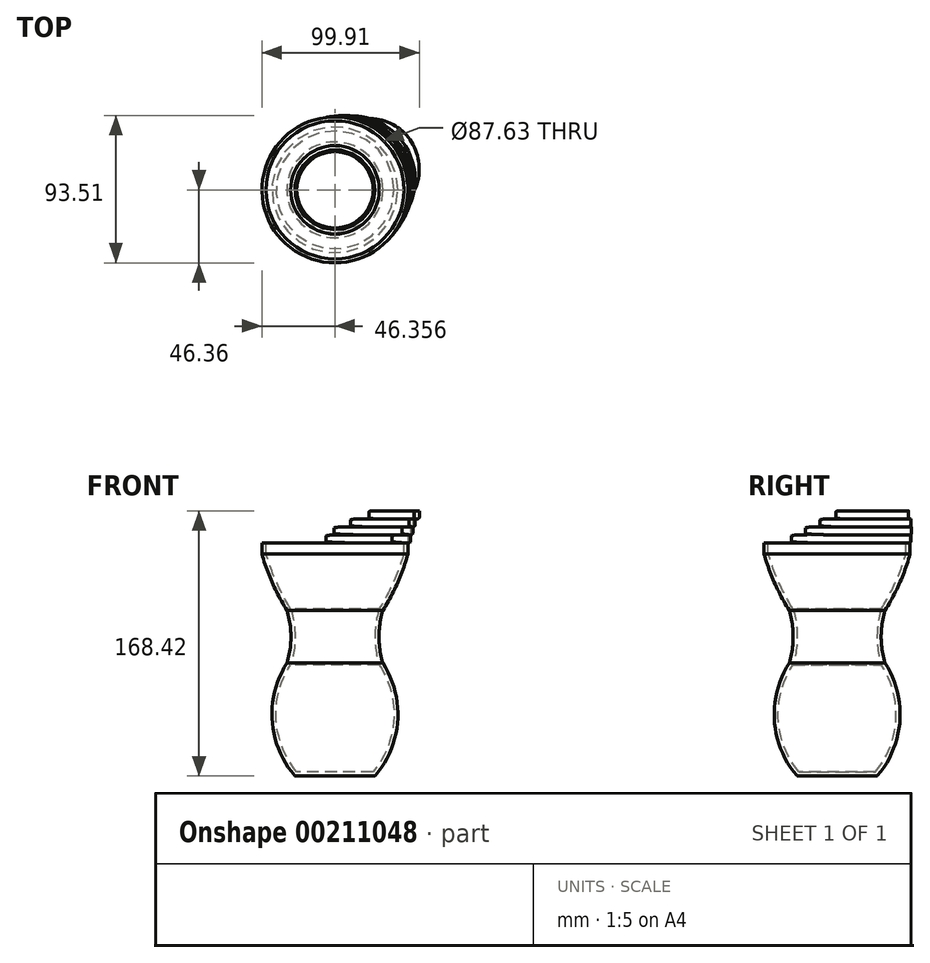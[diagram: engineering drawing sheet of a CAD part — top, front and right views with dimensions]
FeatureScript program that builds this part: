
annotation { "Feature Type Name" : "Feature", "Feature Type Description" : "" }
export const myFeature = defineFeature(function(context is Context, id is Id, definition is map)
    precondition{}
    {
        {
            var Q0;
            Q0=qCreatedBy(makeId("Front.planeOp"),FACE);
            var sketch = newSketch(context, id + "F0", { "sketchPlane" : qUnion([Q0])});
            skLineSegment(sketch, "E0", {"start": v(-425.9, -19.23) * mm, "end": v(-425.9, -160.2) * mm});
            skLineSegment(sketch, "E1", {"start": v(-425.9, -160.2) * mm, "end": v(-451.3, -160.2) * mm});
            skLineSegment(sketch, "E2", {"start": v(-472.26, -19.23) * mm, "end": v(-425.9, -19.23) * mm});
            skArc(sketch, "E3", {"start": v(-456.34, -88.54) * mm, "mid": v(-453.84, -71.81) * mm, "end": v(-456.34, -55.09) * mm});
            skArc(sketch, "E4", {"start": v(-456.34, -88.54) * mm, "mid": v(-465.76, -125.2) * mm, "end": v(-451.3, -160.2) * mm});
            skArc(sketch, "E5", {"start": v(-472.26, -19.23) * mm, "mid": v(-465.56, -37.72) * mm, "end": v(-456.34, -55.09) * mm});
            skLineSegment(sketch, "E6", {"start": v(-425.9, -19.23) * mm, "end": v(-425.9, -12.1) * mm});
            skLineSegment(sketch, "E7", {"start": v(-472.26, -19.23) * mm, "end": v(-472.26, -12.1) * mm});
            skLineSegment(sketch, "E8", {"start": v(-472.26, -12.1) * mm, "end": v(-425.9, -12.1) * mm});
            skSolve(sketch);
        }
        {
            var Q0;
            Q0=makeQuery(id+"F0.imprint","IMPRINT",FACE,{"disambiguationData":[TD([[makeQuery(id+"F0.imprint","IMPRINT",EDGE,{"derivedFrom":sQuery(id+"F0.wireOp",EDGE,"E0")}),-1.0]])]});
            var Q1;
            Q1=makeQuery(id+"F0.imprint","IMPRINT",FACE,{"disambiguationData":[TD([[makeQuery(id+"F0.imprint","IMPRINT",EDGE,{"derivedFrom":sQuery(id+"F0.wireOp",EDGE,"E2")}),1.0]])]});
            var Q2;
            Q2=sQuery(id+"F0.wireOp",EDGE,"E0");
            revolve(context, id + "F1", {"entities" : qUnion([Q0, Q1]), "axis" : qUnion([Q2]), "revolveType" : RevolveType.FULL});
        }
        {
            var Q0;
            Q0=makeQuery(id+"F1.opRevolve","SWEPT_FACE",FACE,{"disambiguationData":[OSD([sQuery(id+"F0.wireOp",EDGE,"E8")])]});
            shell(context, id + "F2", {"entities" : qUnion([Q0]), "thickness" : 2.54 * mm});
        }
        {
            var Q0;
            Q0=makeQuery(id+"F1.opRevolve","SWEPT_FACE",FACE,{"disambiguationData":[OSD([sQuery(id+"F0.wireOp",EDGE,"E8")])]});
            var sketch = newSketch(context, id + "F3", { "sketchPlane" : qUnion([Q0])});
            skArc(sketch, "E9", {"start": v(-389.73, -29) * mm, "mid": v(-383.55, 23.65) * mm, "end": v(-431.6, 46) * mm});
            skSolve(sketch);
        }
        {
            var Q0;
            {var subQ0=sQuery(id+"F3.wireOp",EDGE,"E9");Q0=makeQuery(id+"F3.imprint","IMPRINT",FACE,{"disambiguationData":[TD([[makeQuery(id+"F3.imprint","IMPRINT",EDGE,{"derivedFrom":subQ0}),1.0]])]});}
            extrude(context, id + "F4", {"entities" : qUnion([Q0]), "depth" : 5.08 * mm});
        }
        {
            var Q0;
            Q0=makeQuery(id+"F4.opExtrude","CAP_FACE",FACE,{"disambiguationData":[OSD([sQuery(id+"F0.wireOp",EDGE,"E7"),sQuery(id+"F0.wireOp",EDGE,"E8"),sQuery(id+"F3.wireOp",EDGE,"E9")])],"isStart":false});
            var sketch = newSketch(context, id + "F5", { "sketchPlane" : qUnion([Q0])});
            skArc(sketch, "E10", {"start": v(-383.3, -20) * mm, "mid": v(-383.5, 27.19) * mm, "end": v(-426.47, 46.7) * mm});
            skSolve(sketch);
        }
        {
            var Q0;
            {var subQ0=sQuery(id+"F5.wireOp",EDGE,"E10");Q0=makeQuery(id+"F5.imprint","IMPRINT",FACE,{"disambiguationData":[TD([[makeQuery(id+"F5.imprint","IMPRINT",EDGE,{"derivedFrom":subQ0}),1.0]])]});}
            extrude(context, id + "F6", {"entities" : qUnion([Q0]), "depth" : 5.08 * mm});
        }
        {
            var Q0;
            Q0=makeQuery(id+"F6.opExtrude","CAP_FACE",FACE,{"disambiguationData":[OSD([sQuery(id+"F3.wireOp",EDGE,"E9"),sQuery(id+"F5.wireOp",EDGE,"E10")])],"isStart":false});
            var sketch = newSketch(context, id + "F7", { "sketchPlane" : qUnion([Q0])});
            skArc(sketch, "E11", {"start": v(-378.91, -10.92) * mm, "mid": v(-381.4, 28.3) * mm, "end": v(-415.99, 46.95) * mm});
            skSolve(sketch);
        }
        {
            var Q0;
            {var subQ0=sQuery(id+"F7.wireOp",EDGE,"E11");Q0=makeQuery(id+"F7.imprint","IMPRINT",FACE,{"disambiguationData":[TD([[makeQuery(id+"F7.imprint","IMPRINT",EDGE,{"derivedFrom":subQ0}),1.0]])]});}
            extrude(context, id + "F8", {"entities" : qUnion([Q0]), "depth" : 5.08 * mm});
        }
        {
            var Q0;
            Q0=makeQuery(id+"F8.opExtrude","CAP_FACE",FACE,{"disambiguationData":[OSD([sQuery(id+"F5.wireOp",EDGE,"E10"),sQuery(id+"F7.wireOp",EDGE,"E11")])],"isStart":false});
            var sketch = newSketch(context, id + "F9", { "sketchPlane" : qUnion([Q0])});
            skArc(sketch, "E12", {"start": v(-375.67, -0.9) * mm, "mid": v(-377.16, 30.22) * mm, "end": v(-404.39, 45.4) * mm});
            skSolve(sketch);
        }
        {
            var Q0;
            {var subQ0=sQuery(id+"F9.wireOp",EDGE,"E12");Q0=makeQuery(id+"F9.imprint","IMPRINT",FACE,{"disambiguationData":[TD([[makeQuery(id+"F9.imprint","IMPRINT",EDGE,{"derivedFrom":subQ0}),1.0]])]});}
            extrude(context, id + "F10", {"entities" : qUnion([Q0]), "depth" : 5.08 * mm});
        }
        {
            var Q0;
            Q0=makeQuery(id+"F6.opExtrude","CAP_EDGE",EDGE,{"disambiguationData":[OSD([sQuery(id+"F3.wireOp",EDGE,"E9")])],"isStart":false});
            var Q1;
            Q1=makeQuery(id+"F4.opExtrude","CAP_EDGE",EDGE,{"disambiguationData":[OSD([sQuery(id+"F0.wireOp",EDGE,"E7"),sQuery(id+"F0.wireOp",EDGE,"E8")])],"isStart":false});
            var Q2;
            Q2=makeQuery(id+"F2.opShell","OFFSET_EDGE",EDGE,{"disambiguationData":[OSD([sQuery(id+"F0.wireOp",EDGE,"E7"),sQuery(id+"F0.wireOp",EDGE,"E8")])]});
            var Q3;
            Q3=makeQuery(id+"F8.opExtrude","CAP_EDGE",EDGE,{"disambiguationData":[OSD([sQuery(id+"F5.wireOp",EDGE,"E10")])],"isStart":false});
            var Q4;
            Q4=makeQuery(id+"F10.opExtrude","CAP_EDGE",EDGE,{"disambiguationData":[OSD([sQuery(id+"F7.wireOp",EDGE,"E11")])],"isStart":false});
            fillet(context, id + "F11", {"entities" : qUnion([Q0, Q1, Q2, Q3, Q4]), "radius" : 0.76 * mm, "tangentPropagation" : true, "allowEdgeOverflow" : false});
        }
        {
            var Q0;
            Q0=makeQuery(id+"F10.opExtrude","CAP_EDGE",EDGE,{"disambiguationData":[OSD([sQuery(id+"F9.wireOp",EDGE,"E12")])],"isStart":true});
            var Q1;
            Q1=makeQuery(id+"F8.opExtrude","CAP_EDGE",EDGE,{"disambiguationData":[OSD([sQuery(id+"F7.wireOp",EDGE,"E11")])],"isStart":true});
            var Q2;
            Q2=makeQuery(id+"F6.opExtrude","CAP_EDGE",EDGE,{"disambiguationData":[OSD([sQuery(id+"F5.wireOp",EDGE,"E10")])],"isStart":true});
            var Q3;
            Q3=makeQuery(id+"F4.opExtrude","CAP_EDGE",EDGE,{"disambiguationData":[OSD([sQuery(id+"F3.wireOp",EDGE,"E9")])],"isStart":true});
            fillet(context, id + "F12", {"entities" : qUnion([Q0, Q1, Q2, Q3]), "radius" : 1.02 * mm, "tangentPropagation" : true, "allowEdgeOverflow" : false});
        }
        {
            var Q0;
            Q0=makeQuery(id+"F1.opRevolve","SWEPT_EDGE",EDGE,{"disambiguationData":[OSD([sQuery(id+"F0.wireOp",EDGE,"E1"),sQuery(id+"F0.wireOp",EDGE,"E4")])]});
            fillet(context, id + "F13", {"entities" : qUnion([Q0]), "radius" : 0.76 * mm, "tangentPropagation" : true, "allowEdgeOverflow" : false});
        }
    });
